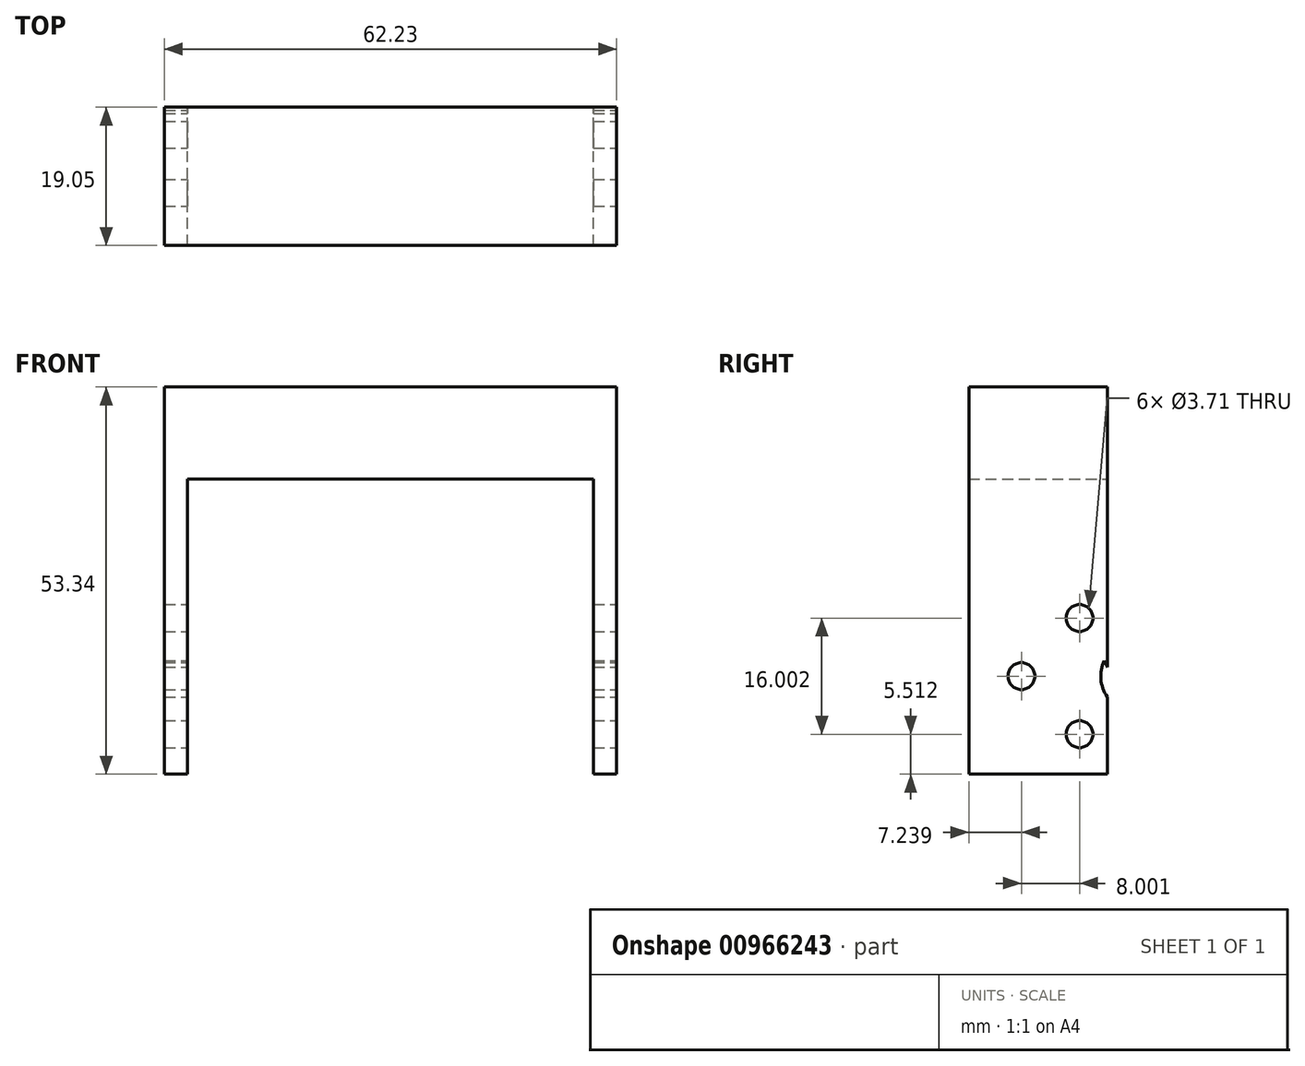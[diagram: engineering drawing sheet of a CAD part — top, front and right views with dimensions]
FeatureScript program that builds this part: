
annotation { "Feature Type Name" : "Feature", "Feature Type Description" : "" }
export const myFeature = defineFeature(function(context is Context, id is Id, definition is map)
    precondition{}
    {
        {
            var Q0;
            Q0=qCreatedBy(makeId("Front.planeOp"),FACE);
            var sketch = newSketch(context, id + "F0", { "sketchPlane" : qUnion([Q0])});
            skLineSegment(sketch, "E0.bottom", {"start": v(0, 0) * mm, "end": v(3.17, 0) * mm});
            skLineSegment(sketch, "E0.top", {"start": v(0, 53.34) * mm, "end": v(62.23, 53.34) * mm});
            skLineSegment(sketch, "E0.left", {"start": v(0, 0) * mm, "end": v(0, 53.34) * mm});
            skLineSegment(sketch, "E0.right", {"start": v(62.23, 0) * mm, "end": v(62.23, 53.34) * mm});
            skLineSegment(sketch, "E1.bottom", {"start": v(3.17, 40.64) * mm, "end": v(59.05, 40.64) * mm});
            skLineSegment(sketch, "E1.top", {"start": v(3.17, 0) * mm, "end": v(59.06, 0) * mm});
            skLineSegment(sketch, "E1.left", {"start": v(3.17, 40.64) * mm, "end": v(3.18, 0) * mm});
            skLineSegment(sketch, "E1.right", {"start": v(59.05, 40.64) * mm, "end": v(59.06, 0) * mm});
            skLineSegment(sketch, "E2.trimOffspring", {"start": v(59.06, 0) * mm, "end": v(62.23, 0) * mm});
            skSolve(sketch);
        }
        {
            var Q0;
            Q0=makeQuery(id+"F0.imprint","IMPRINT",FACE,{"disambiguationData":[TD([[makeQuery(id+"F0.imprint","IMPRINT",EDGE,{"derivedFrom":sQuery(id+"F0.wireOp",EDGE,"E0.bottom")}),1.0]])]});
            extrude(context, id + "F1", {"entities" : qUnion([Q0]), "depth" : 19.05 * mm});
        }
        {
            var Q0;
            Q0=makeQuery(id+"F1.opExtrude","SWEPT_FACE",FACE,{"disambiguationData":[OSD([sQuery(id+"F0.wireOp",EDGE,"E0.right")])]});
            var sketch = newSketch(context, id + "F2", { "sketchPlane" : qUnion([Q0])});
            skCircle(sketch, "E3", {"center": v(-3.81, 13.51) * mm, "radius": 4 * mm});
            skCircle(sketch, "E4", {"center": v(-3.81, 21.51) * mm, "radius": 1.85 * mm});
            skCircle(sketch, "E5", {"center": v(-11.81, 13.51) * mm, "radius": 1.85 * mm});
            skCircle(sketch, "E6", {"center": v(-3.81, 5.51) * mm, "radius": 1.85 * mm});
            skCircle(sketch, "E7", {"center": v(4.2, 13.51) * mm, "radius": 5.08 * mm});
            skLineSegment(sketch, "E8.0.0", {"start": v(0, 0) * mm, "end": v(0, 53.34) * mm});
            skLineSegment(sketch, "E8.0.1", {"start": v(0, 53.34) * mm, "end": v(-19.05, 53.34) * mm});
            skLineSegment(sketch, "E8.0.2", {"start": v(-19.05, 53.34) * mm, "end": v(-19.05, 0) * mm});
            skLineSegment(sketch, "E8.0.3", {"start": v(-19.05, 0) * mm, "end": v(0, 0) * mm});
            skSolve(sketch);
        }
        {
            var Q0;
            {var subQ0=sQuery(id+"F2.wireOp",EDGE,"E8.0.0");var subQ1=sQuery(id+"F2.wireOp",EDGE,"E3");var subQ2=makeQuery(id+"F2.imprint","INTERSECT",VERTEX,{"disambiguationData":[OD(0.0)],"derivedFrom":[subQ1,subQ0]});Q0=makeQuery(id+"F2.imprint","IMPRINT",FACE,{"disambiguationData":[TD([[makeQuery(id+"F2.imprint","IMPRINT",EDGE,{"disambiguationData":[TD([[subQ2,1.0]])],"derivedFrom":subQ1}),-1.0]])]});}
            var Q1;
            Q1=makeQuery(id+"F2.imprint","IMPRINT",FACE,{"disambiguationData":[TD([[makeQuery(id+"F2.imprint","IMPRINT",EDGE,{"derivedFrom":sQuery(id+"F2.wireOp",EDGE,"E4")}),1.0]])]});
            var Q2;
            Q2=makeQuery(id+"F2.imprint","IMPRINT",FACE,{"disambiguationData":[TD([[makeQuery(id+"F2.imprint","IMPRINT",EDGE,{"derivedFrom":sQuery(id+"F2.wireOp",EDGE,"E5")}),1.0]])]});
            var Q3;
            Q3=makeQuery(id+"F2.imprint","IMPRINT",FACE,{"disambiguationData":[TD([[makeQuery(id+"F2.imprint","IMPRINT",EDGE,{"derivedFrom":sQuery(id+"F2.wireOp",EDGE,"E6")}),1.0]])]});
            var Q4;
            {var subQ0=sQuery(id+"F2.wireOp",EDGE,"E8.0.0");var subQ1=sQuery(id+"F2.wireOp",EDGE,"E3");var subQ2=makeQuery(id+"F2.imprint","INTERSECT",VERTEX,{"disambiguationData":[OD(0.0)],"derivedFrom":[subQ1,subQ0]});Q4=makeQuery(id+"F2.imprint","IMPRINT",FACE,{"disambiguationData":[TD([[makeQuery(id+"F2.imprint","IMPRINT",EDGE,{"disambiguationData":[TD([[subQ2,1.0]])],"derivedFrom":subQ1}),1.0]])]});}
            extrude(context, id + "F3", {"entities" : qUnion([Q0, Q1, Q2, Q3, Q4]), "operationType" : NewBodyOperationType.REMOVE, "endBound" : BoundingType.THROUGH_ALL, "oppositeDirection" : true, "depth" : 25.4 * mm});
        }
    });
